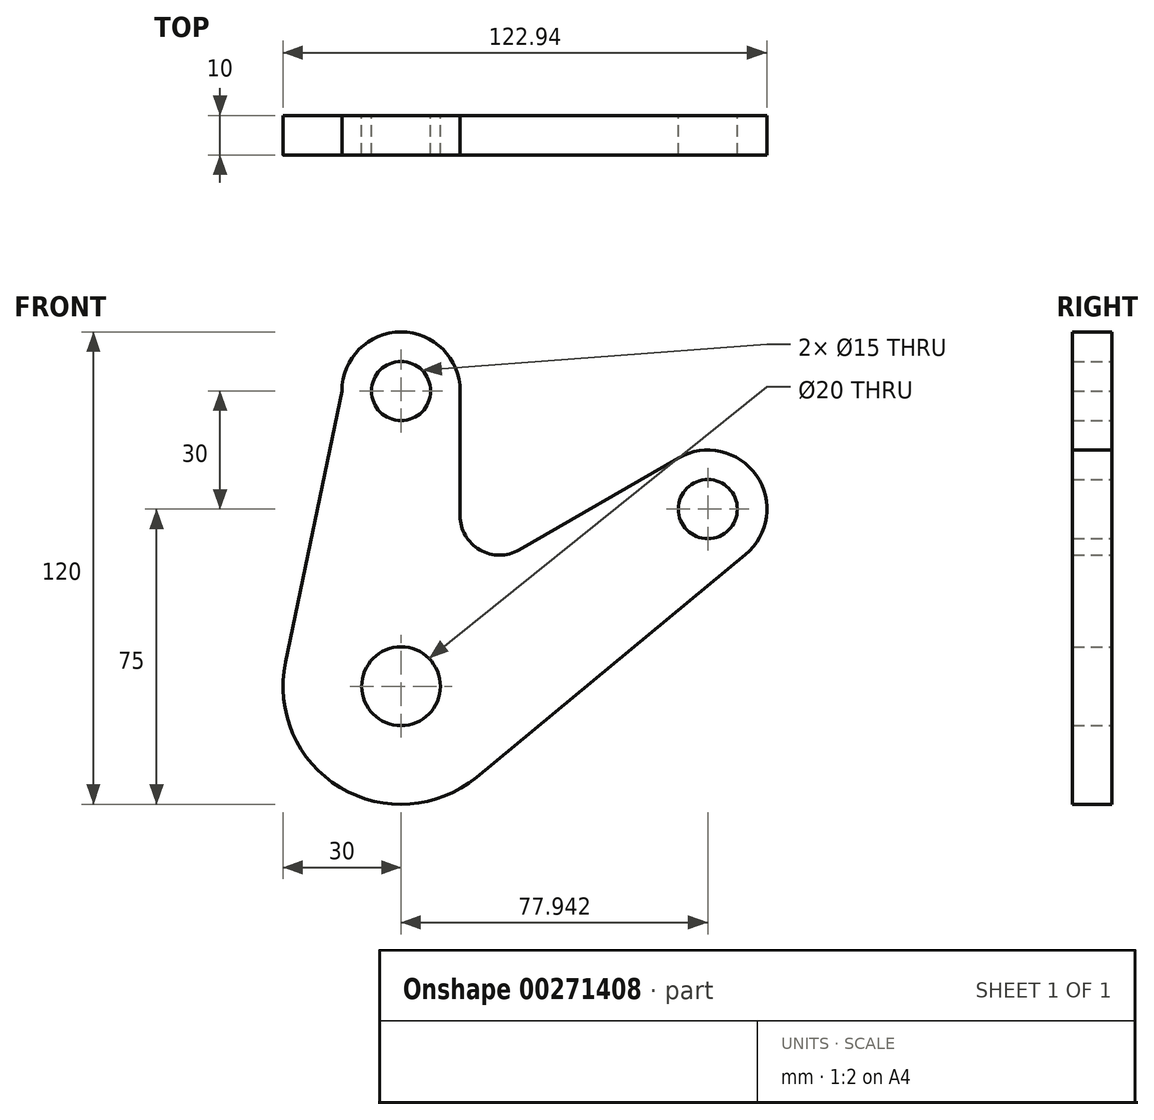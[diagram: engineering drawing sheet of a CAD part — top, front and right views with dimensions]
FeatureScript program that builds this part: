
annotation { "Feature Type Name" : "Feature", "Feature Type Description" : "" }
export const myFeature = defineFeature(function(context is Context, id is Id, definition is map)
    precondition{}
    {
        {
            var Q0;
            Q0=qCreatedBy(makeId("Front.planeOp"),FACE);
            var sketch = newSketch(context, id + "F0", { "sketchPlane" : qUnion([Q0])});
            skCircle(sketch, "E0", {"center": v(0, 0) * mm, "radius": 10 * mm});
            skCircle(sketch, "E1", {"center": v(0, 75) * mm, "radius": 7.5 * mm});
            skCircle(sketch, "E2", {"center": v(77.94, 45) * mm, "radius": 7.5 * mm});
            skArc(sketch, "E3", {"start": v(-29.37, 6.13) * mm, "mid": v(-15.5, -25.69) * mm, "end": v(19.12, -23.12) * mm});
            skLineSegment(sketch, "E4", {"start": v(-15, 75) * mm, "end": v(-29.37, 6.13) * mm});
            skArc(sketch, "E5", {"start": v(15, 75) * mm, "mid": v(0, 90) * mm, "end": v(-15, 75) * mm});
            skLineSegment(sketch, "E6", {"start": v(19.12, -23.12) * mm, "end": v(87.5, 33.44) * mm});
            skLineSegment(sketch, "E7", {"start": v(0, 75) * mm, "end": v(0, 0) * mm, "construction": true});
            skLineSegment(sketch, "E8", {"start": v(0, 0) * mm, "end": v(77.94, 45) * mm, "construction": true});
            skLineSegment(sketch, "E9", {"start": v(15, 75) * mm, "end": v(15, 43.3) * mm});
            skArc(sketch, "E10", {"start": v(15, 43.3) * mm, "mid": v(20, 34.64) * mm, "end": v(30, 34.64) * mm});
            skLineSegment(sketch, "E11", {"start": v(30, 34.64) * mm, "end": v(70.44, 58) * mm});
            skArc(sketch, "E12", {"start": v(87.5, 33.44) * mm, "mid": v(90.26, 53.56) * mm, "end": v(70.44, 58) * mm});
            skSolve(sketch);
        }
        {
            var Q0;
            Q0 = qSketchRegion(id + "F0", true);
            extrude(context, id + "F1", {"entities" : qUnion([Q0]), "depth" : 10 * mm});
        }
    });
